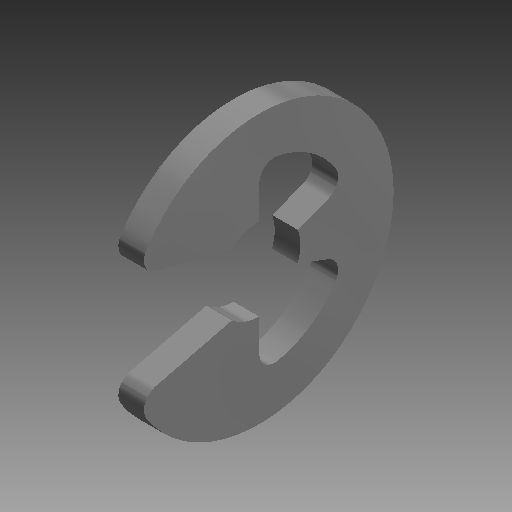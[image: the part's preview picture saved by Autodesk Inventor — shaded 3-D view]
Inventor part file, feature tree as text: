
AUTODESK INVENTOR PART (.ipt)
format: ipt  version: 2019 (Build 230136000, 136)  size: 90,112 bytes
history: native  units: mm (DEFAULTED — no unit token found)
features: fillet x1
ambient origin geometry x8: Origin, YZ Plane, XZ Plane, XY Plane, X Axis, Y Axis, Z Axis, Center Point
bodies: Solid1 (feature_tree)
feature tree (1):
  fillet  "Fillet1"  [1 undecoded]
note: 1 required parameter value undecoded (feature->parameter linkage not recoverable at this tier; creation-order binding heuristic only, values carry confidence <= 0.55)
